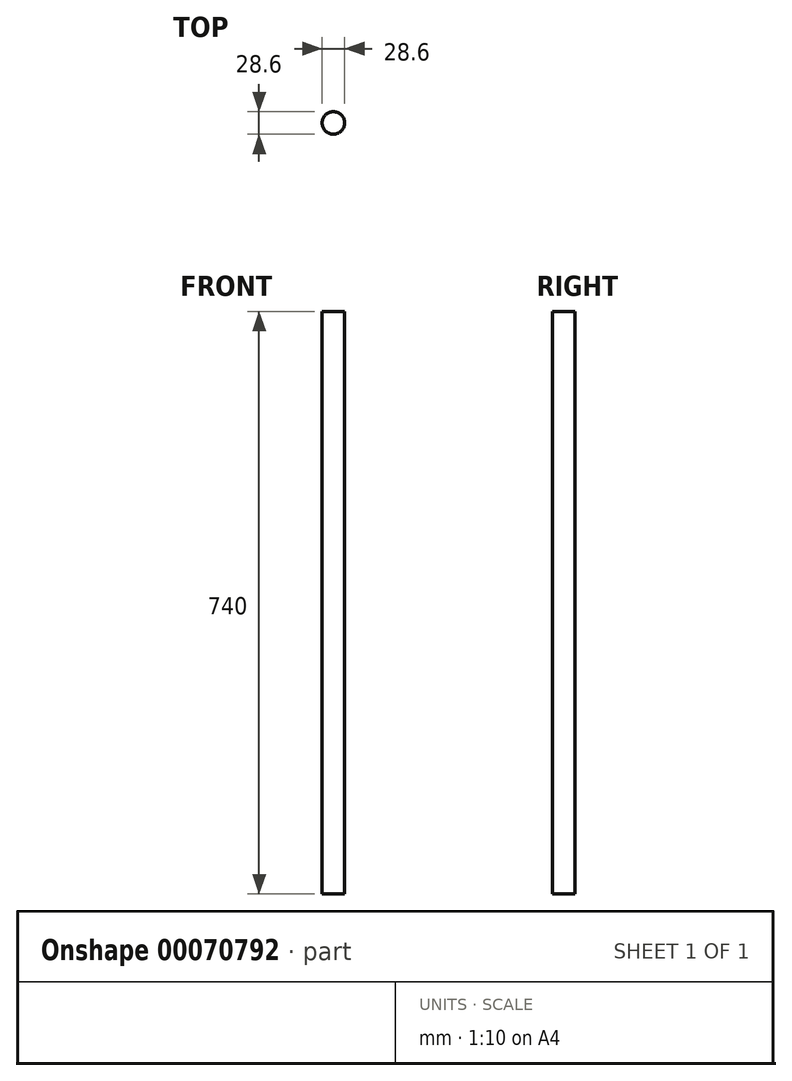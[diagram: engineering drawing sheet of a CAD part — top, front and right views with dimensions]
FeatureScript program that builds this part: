
annotation { "Feature Type Name" : "Feature", "Feature Type Description" : "" }
export const myFeature = defineFeature(function(context is Context, id is Id, definition is map)
    precondition{}
    {
        {
            var Q0;
            Q0=qCreatedBy(makeId("Top.planeOp"),FACE);
            var sketch = newSketch(context, id + "F0", { "sketchPlane" : qUnion([Q0])});
            skCircle(sketch, "E0", {"center": v(0, 0) * mm, "radius": 14.3 * mm});
            skSolve(sketch);
        }
        {
            var Q0;
            Q0=makeQuery(id+"F0.imprint","IMPRINT",FACE,{"disambiguationData":[TD([[makeQuery(id+"F0.imprint","IMPRINT",EDGE,{"derivedFrom":sQuery(id+"F0.wireOp",EDGE,"E0")}),1.0]])]});
            extrude(context, id + "F1", {"entities" : qUnion([Q0]), "depth" : 740 * mm});
        }
    });
